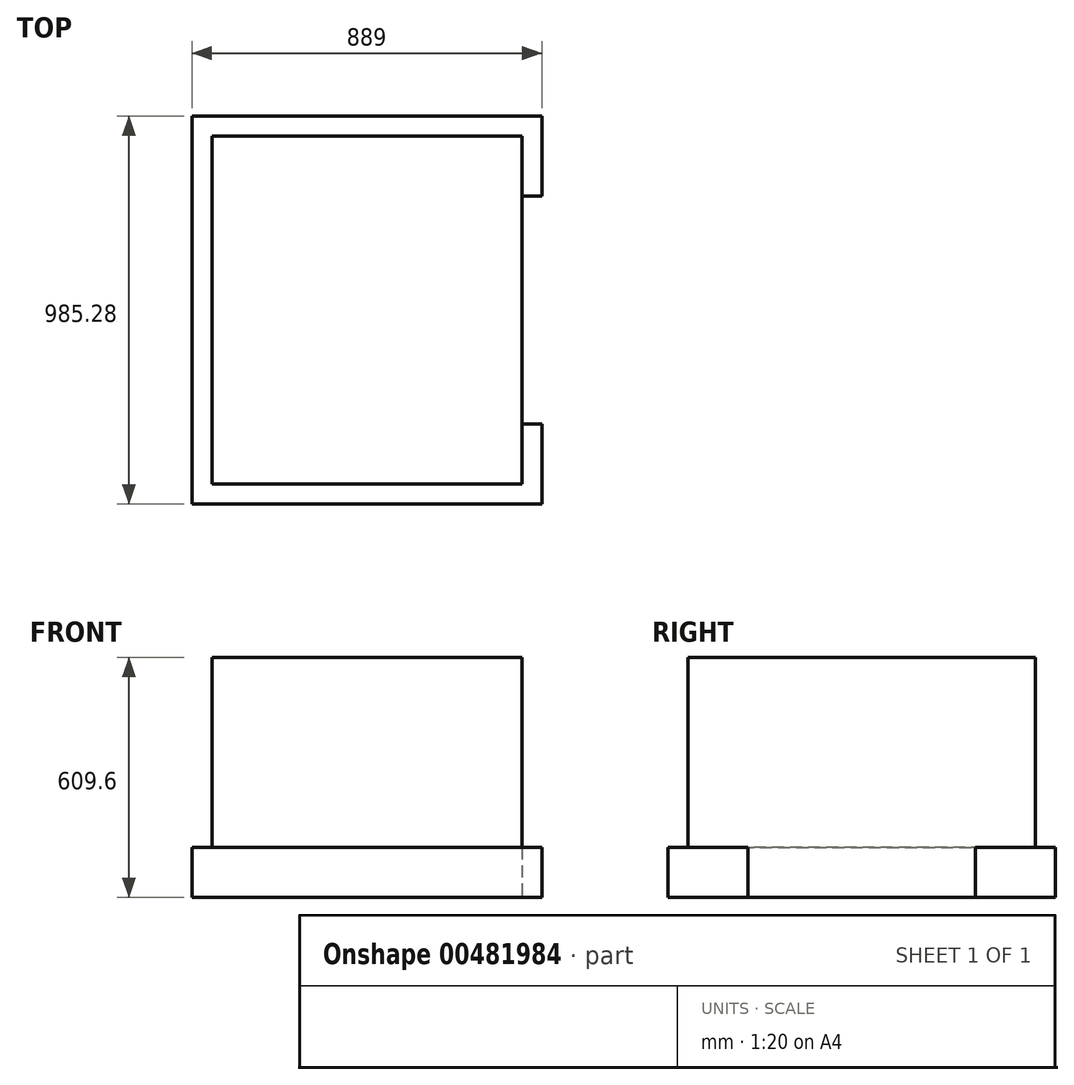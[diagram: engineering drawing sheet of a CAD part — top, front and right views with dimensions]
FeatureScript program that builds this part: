
annotation { "Feature Type Name" : "Feature", "Feature Type Description" : "" }
export const myFeature = defineFeature(function(context is Context, id is Id, definition is map)
    precondition{}
    {
        {
            var Q0;
            Q0=qCreatedBy(makeId("Top.planeOp"),FACE);
            var sketch = newSketch(context, id + "F0", { "sketchPlane" : qUnion([Q0])});
            skLineSegment(sketch, "E0.bottom", {"start": v(-480.28, 760.43) * mm, "end": v(434.12, 760.43) * mm});
            skLineSegment(sketch, "E0.top", {"start": v(-480.28, -255.57) * mm, "end": v(434.12, -255.57) * mm});
            skLineSegment(sketch, "E0.left", {"start": v(-480.28, 760.43) * mm, "end": v(-480.28, -255.57) * mm});
            skLineSegment(sketch, "E0.right", {"start": v(434.12, 760.43) * mm, "end": v(434.12, -255.57) * mm});
            skSolve(sketch);
        }
        {
            var Q0;
            Q0=qCreatedBy(makeId("Top.planeOp"),FACE);
            var sketch = newSketch(context, id + "F1", { "sketchPlane" : qUnion([Q0])});
            skLineSegment(sketch, "E1", {"start": v(-466.46, 747.73) * mm, "end": v(-466.46, -242.87) * mm});
            skLineSegment(sketch, "E2", {"start": v(-466.46, -242.87) * mm, "end": v(422.54, -242.87) * mm});
            skLineSegment(sketch, "E3", {"start": v(422.54, -242.87) * mm, "end": v(422.54, -39.67) * mm});
            skLineSegment(sketch, "E4", {"start": v(422.54, -39.67) * mm, "end": v(371.74, -39.67) * mm});
            skLineSegment(sketch, "E5", {"start": v(371.74, -39.67) * mm, "end": v(371.74, -192.07) * mm});
            skLineSegment(sketch, "E6", {"start": v(371.74, -192.07) * mm, "end": v(-415.66, -192.07) * mm});
            skLineSegment(sketch, "E7", {"start": v(-415.66, -192.07) * mm, "end": v(-415.66, 691.6) * mm});
            skLineSegment(sketch, "E8", {"start": v(-415.66, 691.6) * mm, "end": v(371.74, 691.6) * mm});
            skLineSegment(sketch, "E9", {"start": v(371.74, 691.6) * mm, "end": v(371.74, 539.2) * mm});
            skLineSegment(sketch, "E10", {"start": v(371.74, 539.2) * mm, "end": v(422.54, 539.2) * mm});
            skLineSegment(sketch, "E11", {"start": v(422.54, 539.2) * mm, "end": v(422.54, 742.4) * mm});
            skLineSegment(sketch, "E12", {"start": v(422.54, 742.4) * mm, "end": v(-466.46, 742.4) * mm});
            skSolve(sketch);
        }
        {
            var Q0;
            Q0 = qSketchRegion(id + "F1", true);
            extrude(context, id + "F2", {"entities" : qUnion([Q0]), "depth" : 127 * mm});
        }
        {
            var Q0;
            Q0=makeQuery(id+"F2.opExtrude","CAP_FACE",FACE,{"disambiguationData":[OSD([sQuery(id+"F1.wireOp",EDGE,"E1"),sQuery(id+"F1.wireOp",EDGE,"E2"),sQuery(id+"F1.wireOp",EDGE,"E3"),sQuery(id+"F1.wireOp",EDGE,"E4"),sQuery(id+"F1.wireOp",EDGE,"E5"),sQuery(id+"F1.wireOp",EDGE,"E6"),sQuery(id+"F1.wireOp",EDGE,"E7"),sQuery(id+"F1.wireOp",EDGE,"E8"),sQuery(id+"F1.wireOp",EDGE,"E9"),sQuery(id+"F1.wireOp",EDGE,"E10"),sQuery(id+"F1.wireOp",EDGE,"E11"),sQuery(id+"F1.wireOp",EDGE,"E12")])],"isStart":true});
            var sketch = newSketch(context, id + "F3", { "sketchPlane" : qUnion([Q0])});
            skLineSegment(sketch, "E13.bottom", {"start": v(371.74, 192.07) * mm, "end": v(-415.66, 192.07) * mm});
            skLineSegment(sketch, "E13.top", {"start": v(371.74, -691.6) * mm, "end": v(-415.66, -691.6) * mm});
            skLineSegment(sketch, "E13.left", {"start": v(371.74, 192.07) * mm, "end": v(371.74, -691.6) * mm});
            skLineSegment(sketch, "E13.right", {"start": v(-415.66, 192.07) * mm, "end": v(-415.66, -691.6) * mm});
            skSolve(sketch);
        }
        {
            var Q0;
            {var subQ2=sQuery(id+"F3.wireOp",EDGE,"E13.bottom");Q0=makeQuery(id+"F3.imprint","IMPRINT",FACE,{"disambiguationData":[TD([[makeQuery(id+"F3.imprint","IMPRINT",EDGE,{"derivedFrom":subQ2}),1.0]])]});}
            extrude(context, id + "F4", {"entities" : qUnion([Q0]), "operationType" : NewBodyOperationType.ADD, "oppositeDirection" : true, "depth" : 609.6 * mm});
        }
    });
